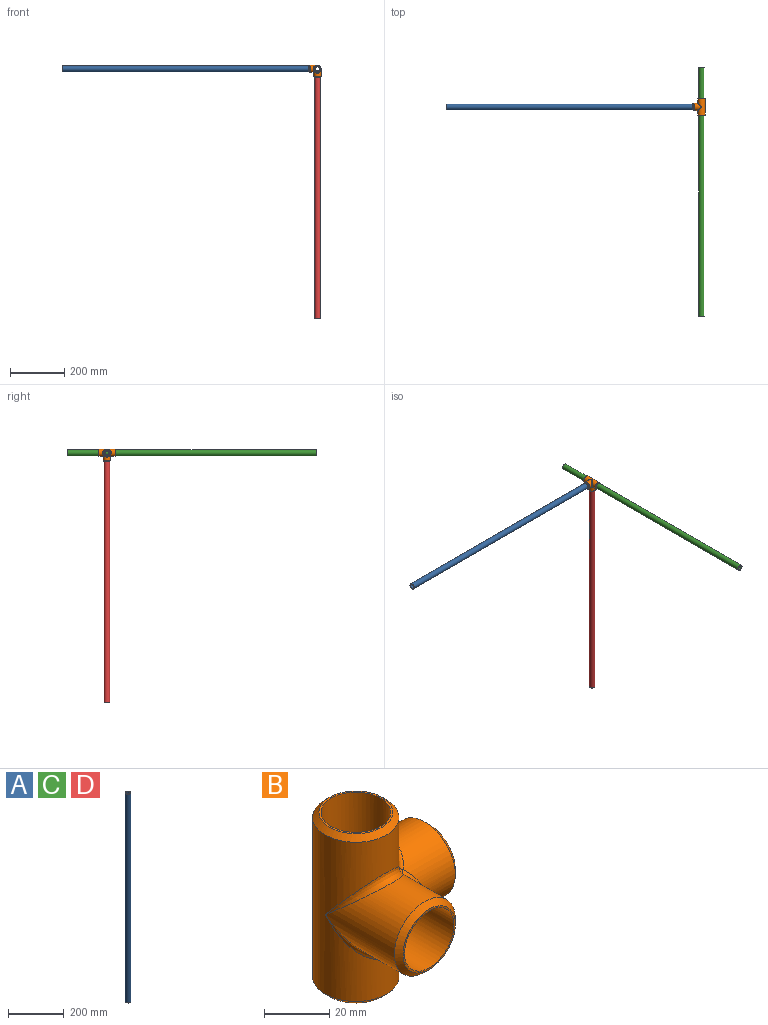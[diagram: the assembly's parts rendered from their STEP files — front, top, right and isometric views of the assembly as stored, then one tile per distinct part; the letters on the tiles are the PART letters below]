
ASSEMBLY  parts=4 mates=3
PART A: 4 faces, bbox 21.3x21.3x914.4 mm
  f0: cylinder r=7.34mm len=914.4mm, axis (0,0,-1), area 42174.3mm2, adj f2,f3
  f1: cylinder r=10.67mm len=914.4mm, axis (0,0,-1), area 61291.3mm2, adj f2,f3
  f2: plane 21.34x21.34mm, normal (0,0,1), area 188.2mm2, adj f0,f1
  f3: plane 21.34x21.34mm, normal (0,0,-1), area 188.2mm2, adj f0,f1
PART B: 21 faces, bbox 45x45x63.5 mm
  f0: cylinder r=10.67mm len=63.5mm, axis (0,0,-1), area 3479.2mm2, adj f1,f4,f5,f6
  f1: cylinder r=10.67mm len=31.75mm, axis (0,1,0), area 1578.7mm2, adj f0,f4,f9
  f2: cylinder r=13.21mm len=59.69mm, axis (0,0,-1), area 3533.3mm2, adj f10,f11,f13,f16,f17,f20
  f3: cylinder r=13.21mm len=29.85mm, axis (-1,0,0), area 1472.5mm2, adj f11,f14,f16,f18
  f4: cylinder r=10.67mm len=31.75mm, axis (-1,0,0), area 1578.7mm2, adj f0,f1,f7
  f5: plane 22.61x22.61mm, normal (0,0,1), area 43.8mm2, adj f0,f20
  f6: plane 22.61x22.61mm, normal (0,0,-1), area 43.8mm2, adj f0,f17
  f7: plane 22.61x22.61mm, normal (1,0,0), area 43.8mm2, adj f4,f18
  f8: cylinder r=13.21mm len=29.85mm, axis (0,1,0), area 1472.5mm2, adj f10,f13,f14,f19
  f9: plane 22.61x22.61mm, normal (0,-1,0), area 43.8mm2, adj f1,f19
  f10: bspline ~22.85x15.75mm, area 98mm2, adj f2,f8,f12
  f11: bspline ~23.69x15.75mm, area 98mm2, adj f2,f3,f12
  f12: sphere r=2.54mm, area 3.6mm2, adj f10,f11,f14
  f13: bspline ~23.69x15.75mm, area 98mm2, adj f2,f8,f15
  f14: bspline ~19.29x6.71mm, area 77.8mm2, adj f3,f8,f12,f15
  f15: sphere r=2.54mm, area 3.6mm2, adj f13,f14,f16
  f16: bspline ~22.85x15.75mm, area 98mm2, adj f2,f3,f15
  f17: cone r=13.21mm half-angle=45deg, axis (0,0,1), area 207.5mm2, adj f2,f6
  f18: cone r=11.3mm half-angle=45deg, axis (-1,0,0), area 207.5mm2, adj f3,f7
  f19: cone r=11.3mm half-angle=45deg, axis (0,1,0), area 207.5mm2, adj f8,f9
  f20: cone r=11.3mm half-angle=45deg, axis (0,0,-1), area 207.5mm2, adj f2,f5
PART C: same geometry as A
PART D: same geometry as A
PLACE A rot(axis=(0.59,-0.55,-0.59),122.6deg) t=(-481.27,-143.62,0)mm fixed
PLACE B rot(axis=(0.58,0.58,-0.58),120deg) t=(0,-143.62,0)mm fixed
PLACE C rot(axis=(0,0.71,0.71),180deg) t=(0,-457.2,0)mm
PLACE D rot(axis=(0,0,1),16.1deg) t=(0,-143.62,-463.58)mm fixed
MATE cylindrical A.f1 <-> B.f1  axis (1,0,0) through (-481.27,-143.62,0)mm
MATE cylindrical C.f1 <-> B.f2  axis (0,-1,0) through (0,0,0)mm
MATE cylindrical B.f4 <-> D.f1  axis (0,0,1) through (0,-143.62,-15.78)mm
